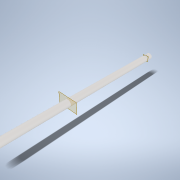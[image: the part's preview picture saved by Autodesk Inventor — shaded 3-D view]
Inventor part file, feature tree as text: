
AUTODESK INVENTOR PART (.ipt)
format: ipt  version: 2021 (Build 250183000, 183)  size: 187,904 bytes
history: native  units: mm
features: other x6, extrude x2, sketch x2, chamfer x1, pattern_linear x1, reference x1
ambient origin geometry x8: Origin, YZ Plane, XZ Plane, XY Plane, X Axis, Y Axis, Z Axis, Center Point
bodies: Body1 (feature_tree)
feature tree (13):
  other  "Bryła1"
  other  "Płaszczyzna konstrukcyjna1"
  extrude  "Wyciągnięcie proste1"  Depth=20.0mm
  chamfer  "Faza1"  Distance=180.0mm
  other  "Płaszczyzna konstrukcyjna2"
  extrude  "Wyciągnięcie proste2"  Depth=2.0mm TaperAngle=45.0deg
  other  "Oś konstrukcyjna1"
  pattern_linear  "Szyk prostokątny1"  Spacing1=-20.0mm  [1 undecoded]
  sketch  "Szkic1"
  reference  "Odniesienie1"
  sketch  "Szkic2"
  other  "zespul12_2.iam"
  other  "shaft:1"
note: 1 required parameter value undecoded (feature->parameter linkage not recoverable at this tier; creation-order binding heuristic only, values carry confidence <= 0.55)
